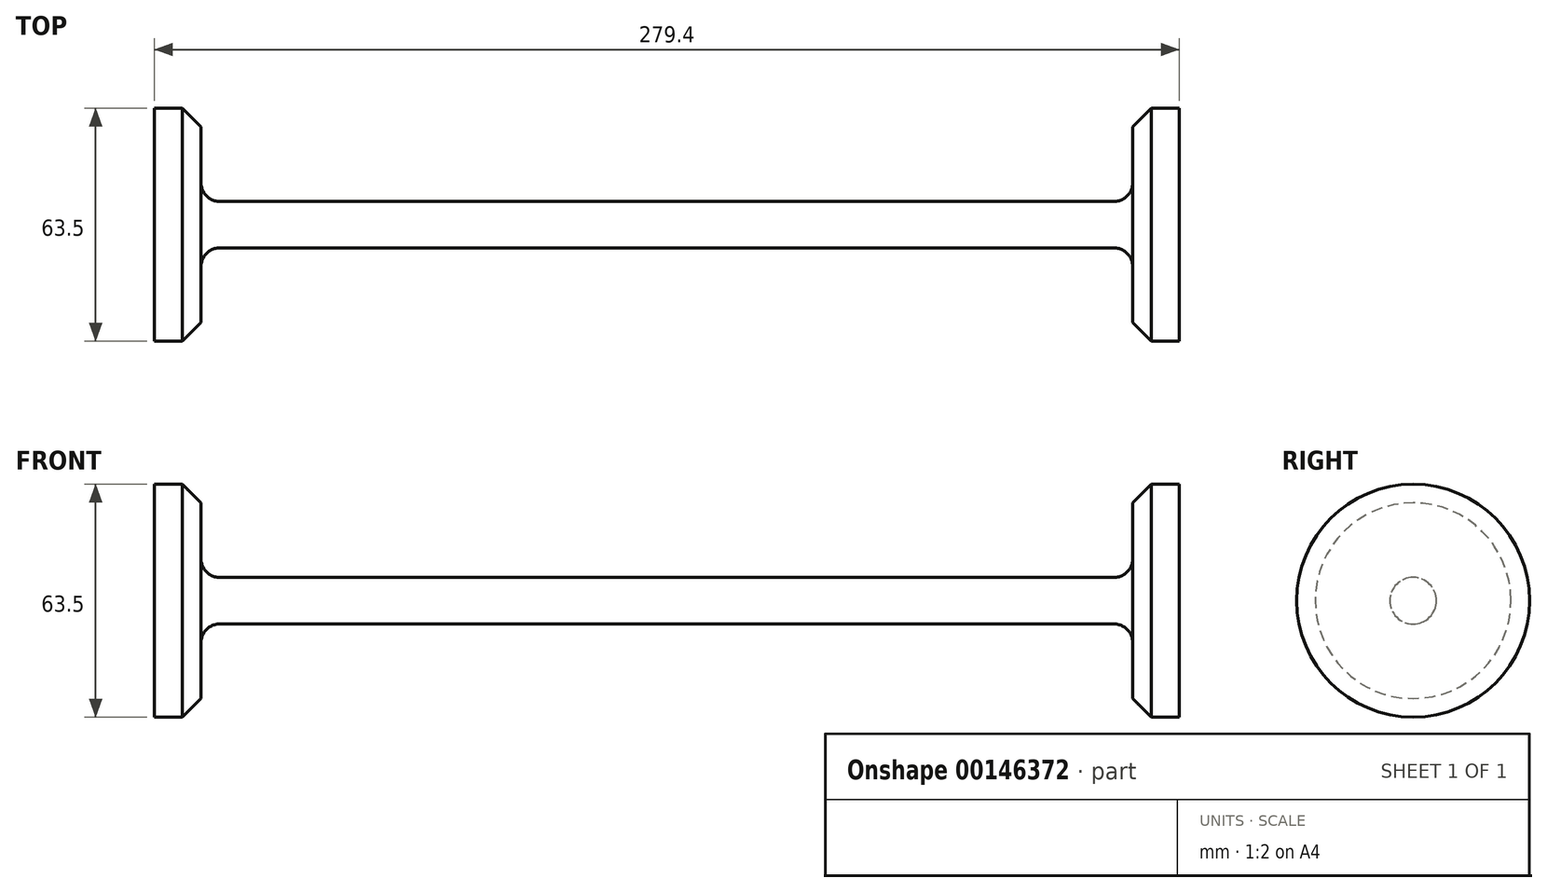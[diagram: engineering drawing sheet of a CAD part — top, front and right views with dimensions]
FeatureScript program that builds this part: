
annotation { "Feature Type Name" : "Feature", "Feature Type Description" : "" }
export const myFeature = defineFeature(function(context is Context, id is Id, definition is map)
    precondition{}
    {
        {
            var Q0;
            Q0=qCreatedBy(makeId("Front.planeOp"),FACE);
            var sketch = newSketch(context, id + "F0", { "sketchPlane" : qUnion([Q0])});
            skLineSegment(sketch, "E0", {"start": v(0, 25.4) * mm, "end": v(12.7, 25.4) * mm});
            skLineSegment(sketch, "E1", {"start": v(12.7, 25.4) * mm, "end": v(12.7, 0) * mm});
            skLineSegment(sketch, "E2", {"start": v(12.7, 0) * mm, "end": v(266.7, 0) * mm});
            skLineSegment(sketch, "E3", {"start": v(266.7, 0) * mm, "end": v(266.7, 25.4) * mm});
            skLineSegment(sketch, "E4", {"start": v(266.7, 25.4) * mm, "end": v(279.4, 25.4) * mm});
            skLineSegment(sketch, "E5", {"start": v(130.34, -6.35) * mm, "end": v(279.4, -6.35) * mm});
            skLineSegment(sketch, "E6", {"start": v(279.4, -6.35) * mm, "end": v(0, -6.35) * mm});
            skLineSegment(sketch, "E7", {"start": v(0, -6.35) * mm, "end": v(0, 25.4) * mm});
            skLineSegment(sketch, "E8", {"start": v(279.4, -6.35) * mm, "end": v(279.4, 25.4) * mm});
            skSolve(sketch);
        }
        {
            var Q0;
            Q0=makeQuery(id+"F0.imprint","IMPRINT",FACE,{"disambiguationData":[TD([[makeQuery(id+"F0.imprint","IMPRINT",EDGE,{"derivedFrom":sQuery(id+"F0.wireOp",EDGE,"E0")}),-1.0]])]});
            var Q1;
            Q1=sQuery(id+"F0.wireOp",EDGE,"E6");
            revolve(context, id + "F1", {"entities" : qUnion([Q0]), "axis" : qUnion([Q1]), "revolveType" : RevolveType.FULL});
        }
        {
            var Q0;
            Q0=makeQuery(id+"F1.opRevolve","SWEPT_EDGE",EDGE,{"disambiguationData":[OSD([sQuery(id+"F0.wireOp",EDGE,"E1"),sQuery(id+"F0.wireOp",EDGE,"E2")])]});
            var Q1;
            Q1=makeQuery(id+"F1.opRevolve","SWEPT_EDGE",EDGE,{"disambiguationData":[OSD([sQuery(id+"F0.wireOp",EDGE,"E2"),sQuery(id+"F0.wireOp",EDGE,"E3")])]});
            fillet(context, id + "F2", {"entities" : qUnion([Q0, Q1]), "radius" : 5.08 * mm, "tangentPropagation" : true, "allowEdgeOverflow" : false});
        }
        {
            var Q0;
            Q0=makeQuery(id+"F1.opRevolve","SWEPT_EDGE",EDGE,{"disambiguationData":[OSD([sQuery(id+"F0.wireOp",EDGE,"E0"),sQuery(id+"F0.wireOp",EDGE,"E1")])]});
            chamfer(context, id + "F3", {"entities" : qUnion([Q0]), "width" : 5.08 * mm, "tangentPropagation" : true});
        }
        {
            var Q0;
            Q0=makeQuery(id+"F1.opRevolve","SWEPT_EDGE",EDGE,{"disambiguationData":[OSD([sQuery(id+"F0.wireOp",EDGE,"E3"),sQuery(id+"F0.wireOp",EDGE,"E4")])]});
            chamfer(context, id + "F4", {"entities" : qUnion([Q0]), "width" : 5.08 * mm, "tangentPropagation" : true});
        }
    });
